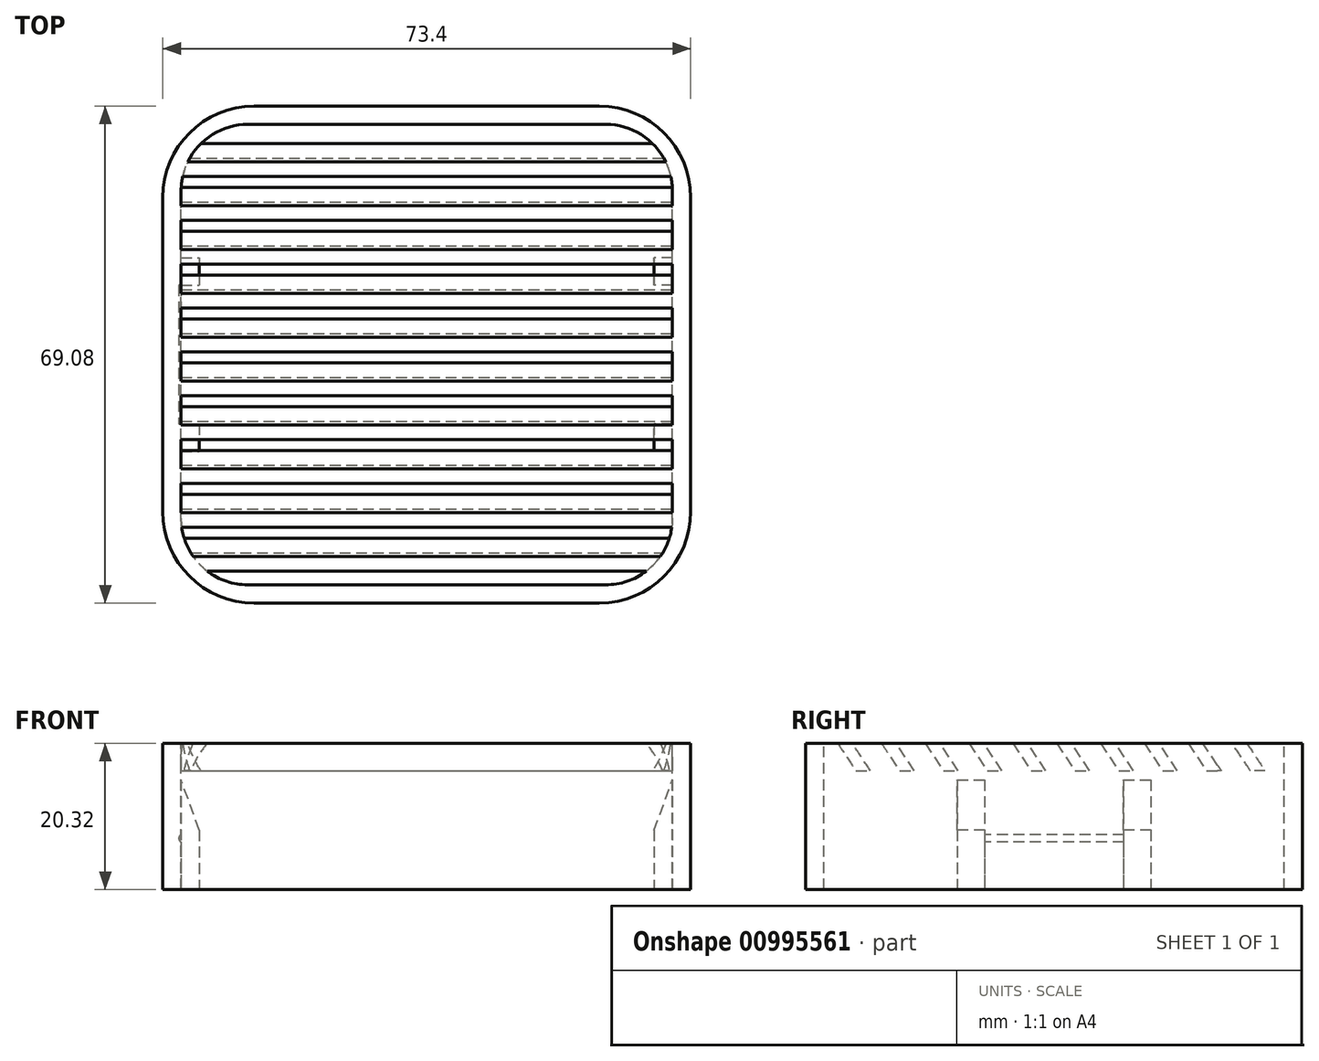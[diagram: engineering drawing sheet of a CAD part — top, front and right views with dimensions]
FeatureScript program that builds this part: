
annotation { "Feature Type Name" : "Feature", "Feature Type Description" : "" }
export const myFeature = defineFeature(function(context is Context, id is Id, definition is map)
    precondition{}
    {
        {
            var Q0;
            Q0=qCreatedBy(makeId("Top.planeOp"),FACE);
            var sketch = newSketch(context, id + "F0", { "sketchPlane" : qUnion([Q0])});
            skLineSegment(sketch, "E0.bottom", {"start": v(36.7, -34.54) * mm, "end": v(-36.7, -34.54) * mm});
            skLineSegment(sketch, "E0.top", {"start": v(36.7, 34.54) * mm, "end": v(-36.7, 34.54) * mm});
            skLineSegment(sketch, "E0.left", {"start": v(36.7, -34.54) * mm, "end": v(36.7, 34.54) * mm});
            skLineSegment(sketch, "E0.right", {"start": v(-36.7, -34.54) * mm, "end": v(-36.7, 34.54) * mm});
            skPoint(sketch, "E0.middle", {"position": v(0, 0) * mm});
            skSolve(sketch);
        }
        {
            var Q0;
            Q0=makeQuery(id+"F0.imprint","IMPRINT",FACE,{"disambiguationData":[TD([[makeQuery(id+"F0.imprint","IMPRINT",EDGE,{"derivedFrom":sQuery(id+"F0.wireOp",EDGE,"E0.bottom")}),-1.0]])]});
            extrude(context, id + "F1", {"entities" : qUnion([Q0]), "depth" : 20.32 * mm, "offsetDistance" : 25.4 * mm});
        }
        {
            var Q0;
            Q0=makeQuery(id+"F1.opExtrude","CAP_FACE",FACE,{"disambiguationData":[OSD([sQuery(id+"F0.wireOp",EDGE,"E0.bottom"),sQuery(id+"F0.wireOp",EDGE,"E0.top"),sQuery(id+"F0.wireOp",EDGE,"E0.left"),sQuery(id+"F0.wireOp",EDGE,"E0.right")])],"isStart":false});
            var sketch = newSketch(context, id + "F2", { "sketchPlane" : qUnion([Q0])});
            skLineSegment(sketch, "E1.0", {"start": v(34.16, 32) * mm, "end": v(-34.16, 32) * mm});
            skLineSegment(sketch, "E1.1", {"start": v(34.16, -32) * mm, "end": v(34.16, 32) * mm});
            skLineSegment(sketch, "E1.2", {"start": v(34.16, -32) * mm, "end": v(-34.16, -32) * mm});
            skLineSegment(sketch, "E1.3", {"start": v(-34.16, -32) * mm, "end": v(-34.16, 32) * mm});
            skSolve(sketch);
        }
        {
            var Q0;
            Q0 = qSketchRegion(id + "F2", true);
            extrude(context, id + "F3", {"entities" : qUnion([Q0]), "operationType" : NewBodyOperationType.REMOVE, "oppositeDirection" : true, "depth" : 25.4 * mm, "offsetDistance" : 25.4 * mm});
        }
        {
            var Q0;
            Q0=makeQuery(id+"F1.opExtrude","SWEPT_FACE",FACE,{"disambiguationData":[OSD([sQuery(id+"F0.wireOp",EDGE,"E0.left")])]});
            var sketch = newSketch(context, id + "F4", { "sketchPlane" : qUnion([Q0])});
            skLineSegment(sketch, "E2", {"start": v(-30.1, 20.32) * mm, "end": v(-27.56, 16.51) * mm});
            skLineSegment(sketch, "E3", {"start": v(-27.56, 16.51) * mm, "end": v(-25.53, 16.51) * mm});
            skLineSegment(sketch, "E4", {"start": v(-25.53, 16.51) * mm, "end": v(-28.07, 20.32) * mm});
            skLineSegment(sketch, "E5", {"start": v(-30.1, 20.32) * mm, "end": v(-28.07, 20.32) * mm});
            skLineSegment(sketch, "E6.1.0.0", {"start": v(-24, 20.32) * mm, "end": v(-21.46, 16.51) * mm});
            skLineSegment(sketch, "E6.1.0.1", {"start": v(-24, 20.32) * mm, "end": v(-21.97, 20.32) * mm});
            skLineSegment(sketch, "E6.1.0.2", {"start": v(-19.43, 16.51) * mm, "end": v(-21.97, 20.32) * mm});
            skLineSegment(sketch, "E6.1.0.3", {"start": v(-21.46, 16.51) * mm, "end": v(-19.43, 16.51) * mm});
            skLineSegment(sketch, "E6.2.0.0", {"start": v(-17.9, 20.32) * mm, "end": v(-15.37, 16.51) * mm});
            skLineSegment(sketch, "E6.2.0.1", {"start": v(-17.9, 20.32) * mm, "end": v(-15.87, 20.32) * mm});
            skLineSegment(sketch, "E6.2.0.2", {"start": v(-13.33, 16.51) * mm, "end": v(-15.87, 20.32) * mm});
            skLineSegment(sketch, "E6.2.0.3", {"start": v(-15.37, 16.51) * mm, "end": v(-13.33, 16.51) * mm});
            skLineSegment(sketch, "E6.3.0.0", {"start": v(-11.81, 20.32) * mm, "end": v(-9.27, 16.51) * mm});
            skLineSegment(sketch, "E6.3.0.1", {"start": v(-11.81, 20.32) * mm, "end": v(-9.78, 20.32) * mm});
            skLineSegment(sketch, "E6.3.0.2", {"start": v(-7.24, 16.51) * mm, "end": v(-9.78, 20.32) * mm});
            skLineSegment(sketch, "E6.3.0.3", {"start": v(-9.27, 16.51) * mm, "end": v(-7.24, 16.51) * mm});
            skLineSegment(sketch, "E6.4.0.0", {"start": v(-5.71, 20.32) * mm, "end": v(-3.17, 16.51) * mm});
            skLineSegment(sketch, "E6.4.0.1", {"start": v(-5.71, 20.32) * mm, "end": v(-3.68, 20.32) * mm});
            skLineSegment(sketch, "E6.4.0.2", {"start": v(-1.14, 16.51) * mm, "end": v(-3.68, 20.32) * mm});
            skLineSegment(sketch, "E6.4.0.3", {"start": v(-3.17, 16.51) * mm, "end": v(-1.14, 16.51) * mm});
            skLineSegment(sketch, "E6.5.0.0", {"start": v(0.38, 20.32) * mm, "end": v(2.92, 16.51) * mm});
            skLineSegment(sketch, "E6.5.0.1", {"start": v(0.38, 20.32) * mm, "end": v(2.41, 20.32) * mm});
            skLineSegment(sketch, "E6.5.0.2", {"start": v(4.95, 16.51) * mm, "end": v(2.41, 20.32) * mm});
            skLineSegment(sketch, "E6.5.0.3", {"start": v(2.92, 16.51) * mm, "end": v(4.95, 16.51) * mm});
            skLineSegment(sketch, "E6.6.0.0", {"start": v(6.48, 20.32) * mm, "end": v(9.02, 16.51) * mm});
            skLineSegment(sketch, "E6.6.0.1", {"start": v(6.48, 20.32) * mm, "end": v(8.5, 20.32) * mm});
            skLineSegment(sketch, "E6.6.0.2", {"start": v(11.05, 16.51) * mm, "end": v(8.5, 20.32) * mm});
            skLineSegment(sketch, "E6.6.0.3", {"start": v(9.02, 16.51) * mm, "end": v(11.05, 16.51) * mm});
            skLineSegment(sketch, "E6.7.0.0", {"start": v(12.57, 20.32) * mm, "end": v(15.11, 16.51) * mm});
            skLineSegment(sketch, "E6.7.0.1", {"start": v(12.57, 20.32) * mm, "end": v(14.6, 20.32) * mm});
            skLineSegment(sketch, "E6.7.0.2", {"start": v(17.15, 16.51) * mm, "end": v(14.6, 20.32) * mm});
            skLineSegment(sketch, "E6.7.0.3", {"start": v(15.11, 16.51) * mm, "end": v(17.15, 16.51) * mm});
            skLineSegment(sketch, "E6.8.0.0", {"start": v(18.67, 20.32) * mm, "end": v(21.2, 16.51) * mm});
            skLineSegment(sketch, "E6.8.0.1", {"start": v(18.67, 20.32) * mm, "end": v(20.7, 20.32) * mm});
            skLineSegment(sketch, "E6.8.0.2", {"start": v(23.24, 16.51) * mm, "end": v(20.7, 20.32) * mm});
            skLineSegment(sketch, "E6.8.0.3", {"start": v(21.2, 16.51) * mm, "end": v(23.24, 16.51) * mm});
            skLineSegment(sketch, "E6.9.0.0", {"start": v(24.77, 20.32) * mm, "end": v(27.3, 16.51) * mm});
            skLineSegment(sketch, "E6.9.0.1", {"start": v(24.77, 20.32) * mm, "end": v(26.8, 20.32) * mm});
            skLineSegment(sketch, "E6.9.0.2", {"start": v(29.34, 16.5) * mm, "end": v(26.8, 20.32) * mm});
            skLineSegment(sketch, "E6.9.0.3", {"start": v(27.3, 16.51) * mm, "end": v(29.34, 16.51) * mm});
            skLineSegment(sketch, "E6.direction1", {"start": v(-27.56, 16.51) * mm, "end": v(-21.46, 16.51) * mm, "construction": true});
            skSolve(sketch);
        }
        {
            var Q0;
            Q0 = qSketchRegion(id + "F4", true);
            extrude(context, id + "F5", {"entities" : qUnion([Q0]), "operationType" : NewBodyOperationType.ADD, "oppositeDirection" : true, "depth" : 73.4 * mm, "offsetDistance" : 25.4 * mm});
        }
        {
            var Q0;
            Q0=makeQuery(id+"F3.boolean.opBoolean","COPY",EDGE,{"derivedFrom":makeQuery(id+"F3.opExtrude","SWEPT_EDGE",EDGE,{"disambiguationData":[OSD([sQuery(id+"F2.wireOp",EDGE,"E1.0"),sQuery(id+"F2.wireOp",EDGE,"E1.3")])]})});
            var Q1;
            Q1=makeQuery(id+"F3.boolean.opBoolean","COPY",EDGE,{"derivedFrom":makeQuery(id+"F3.opExtrude","SWEPT_EDGE",EDGE,{"disambiguationData":[OSD([sQuery(id+"F2.wireOp",EDGE,"E1.0"),sQuery(id+"F2.wireOp",EDGE,"E1.1")])]})});
            var Q2;
            Q2=makeQuery(id+"F3.boolean.opBoolean","COPY",EDGE,{"derivedFrom":makeQuery(id+"F3.opExtrude","SWEPT_EDGE",EDGE,{"disambiguationData":[OSD([sQuery(id+"F2.wireOp",EDGE,"E1.1"),sQuery(id+"F2.wireOp",EDGE,"E1.2")])]})});
            var Q3;
            Q3=makeQuery(id+"F3.boolean.opBoolean","COPY",EDGE,{"derivedFrom":makeQuery(id+"F3.opExtrude","SWEPT_EDGE",EDGE,{"disambiguationData":[OSD([sQuery(id+"F2.wireOp",EDGE,"E1.2"),sQuery(id+"F2.wireOp",EDGE,"E1.3")])]})});
            fillet(context, id + "F6", {"entities" : qUnion([Q0, Q1, Q2, Q3]), "radius" : 9.27 * mm, "tangentPropagation" : true, "allowEdgeOverflow" : false});
        }
        {
            var Q0;
            Q0=makeQuery(id+"F1.opExtrude","SWEPT_EDGE",EDGE,{"disambiguationData":[OSD([sQuery(id+"F0.wireOp",EDGE,"E0.bottom"),sQuery(id+"F0.wireOp",EDGE,"E0.left")])]});
            var Q1;
            Q1=makeQuery(id+"F1.opExtrude","SWEPT_EDGE",EDGE,{"disambiguationData":[OSD([sQuery(id+"F0.wireOp",EDGE,"E0.top"),sQuery(id+"F0.wireOp",EDGE,"E0.left")])]});
            var Q2;
            Q2=makeQuery(id+"F1.opExtrude","SWEPT_EDGE",EDGE,{"disambiguationData":[OSD([sQuery(id+"F0.wireOp",EDGE,"E0.bottom"),sQuery(id+"F0.wireOp",EDGE,"E0.right")])]});
            var Q3;
            Q3=makeQuery(id+"F1.opExtrude","SWEPT_EDGE",EDGE,{"disambiguationData":[OSD([sQuery(id+"F0.wireOp",EDGE,"E0.top"),sQuery(id+"F0.wireOp",EDGE,"E0.right")])]});
            fillet(context, id + "F7", {"entities" : qUnion([Q0, Q1, Q2, Q3]), "radius" : 12.7 * mm, "tangentPropagation" : true, "allowEdgeOverflow" : false});
        }
        {
            var Q0;
            Q0=qCreatedBy(makeId("Front.planeOp"),FACE);
            var sketch = newSketch(context, id + "F8", { "sketchPlane" : qUnion([Q0])});
            skLineSegment(sketch, "E7", {"start": v(0, 7.62) * mm, "end": v(-34.16, 7.62) * mm});
            skCircle(sketch, "E8", {"center": v(-33.9, 7.11) * mm, "radius": 0.57 * mm});
            skCircle(sketch, "E9.MirrorC", {"center": v(33.9, 7.11) * mm, "radius": 0.57 * mm});
            skSolve(sketch);
        }
        {
            var Q0;
            {var subQ0=sQuery(id+"F8.wireOp",EDGE,"E8");var subQ1=sQuery(id+"F8.wireOp",EDGE,"E7");var subQ2=makeQuery(id+"F8.imprint","INTERSECT",VERTEX,{"disambiguationData":[OD(0.0)],"derivedFrom":[subQ1,subQ0]});Q0=makeQuery(id+"F8.imprint","IMPRINT",FACE,{"disambiguationData":[TD([[makeQuery(id+"F8.imprint","IMPRINT",EDGE,{"disambiguationData":[TD([[subQ2,1.0]])],"derivedFrom":subQ1}),1.0]])]});}
            var Q1;
            Q1=makeQuery(id+"F8.imprint","IMPRINT",FACE,{"disambiguationData":[TD([[makeQuery(id+"F8.imprint","IMPRINT",EDGE,{"derivedFrom":sQuery(id+"F8.wireOp",EDGE,"E9.MirrorC")}),-1.0]])]});
            extrude(context, id + "F9", {"entities" : qUnion([Q0, Q1]), "operationType" : NewBodyOperationType.REMOVE, "endBound" : BoundingType.SYMMETRIC, "oppositeDirection" : true, "depth" : 19.3 * mm, "offsetDistance" : 25.4 * mm});
        }
        {
            var Q0;
            Q0=makeQuery(id+"F1.opExtrude","CAP_FACE",FACE,{"disambiguationData":[OSD([sQuery(id+"F0.wireOp",EDGE,"E0.bottom"),sQuery(id+"F0.wireOp",EDGE,"E0.top"),sQuery(id+"F0.wireOp",EDGE,"E0.left"),sQuery(id+"F0.wireOp",EDGE,"E0.right")])],"isStart":true});
            var sketch = newSketch(context, id + "F10", { "sketchPlane" : qUnion([Q0])});
            skLineSegment(sketch, "E10.bottom", {"start": v(-34.16, 9.65) * mm, "end": v(-31.62, 9.65) * mm});
            skLineSegment(sketch, "E10.top", {"start": v(-34.16, 13.46) * mm, "end": v(-31.62, 13.46) * mm});
            skLineSegment(sketch, "E10.left", {"start": v(-34.16, 9.65) * mm, "end": v(-34.16, 13.46) * mm});
            skLineSegment(sketch, "E10.right", {"start": v(-31.62, 9.65) * mm, "end": v(-31.62, 13.46) * mm});
            skLineSegment(sketch, "E11.bottom", {"start": v(-34.16, -13.46) * mm, "end": v(-31.62, -13.46) * mm});
            skLineSegment(sketch, "E11.top", {"start": v(-34.16, -9.65) * mm, "end": v(-31.62, -9.65) * mm});
            skLineSegment(sketch, "E11.left", {"start": v(-34.16, -13.46) * mm, "end": v(-34.16, -9.65) * mm});
            skLineSegment(sketch, "E11.right", {"start": v(-31.62, -13.46) * mm, "end": v(-31.62, -9.65) * mm});
            skLineSegment(sketch, "E12.MirrorCS", {"start": v(31.62, 9.65) * mm, "end": v(31.62, 13.46) * mm});
            skLineSegment(sketch, "E13.MirrorCS", {"start": v(34.16, 13.46) * mm, "end": v(31.62, 13.46) * mm});
            skLineSegment(sketch, "E14.MirrorCS", {"start": v(34.16, 9.65) * mm, "end": v(34.16, 13.46) * mm});
            skLineSegment(sketch, "E15.MirrorCS", {"start": v(34.16, 9.65) * mm, "end": v(31.62, 9.65) * mm});
            skLineSegment(sketch, "E16.MirrorCS", {"start": v(34.16, -9.65) * mm, "end": v(31.62, -9.65) * mm});
            skLineSegment(sketch, "E17.MirrorCS", {"start": v(34.16, -13.46) * mm, "end": v(34.16, -9.65) * mm});
            skLineSegment(sketch, "E18.MirrorCS", {"start": v(34.16, -13.46) * mm, "end": v(31.62, -13.46) * mm});
            skLineSegment(sketch, "E19.MirrorCS", {"start": v(31.62, -13.46) * mm, "end": v(31.62, -9.65) * mm});
            skSolve(sketch);
        }
        {
            var Q0;
            Q0=makeQuery(id+"F10.imprint","IMPRINT",FACE,{"disambiguationData":[TD([[makeQuery(id+"F10.imprint","IMPRINT",EDGE,{"derivedFrom":sQuery(id+"F10.wireOp",EDGE,"E10.bottom")}),1.0]])]});
            var Q1;
            Q1=makeQuery(id+"F10.imprint","IMPRINT",FACE,{"disambiguationData":[TD([[makeQuery(id+"F10.imprint","IMPRINT",EDGE,{"derivedFrom":sQuery(id+"F10.wireOp",EDGE,"E11.bottom")}),1.0]])]});
            var Q2;
            Q2=makeQuery(id+"F10.imprint","IMPRINT",FACE,{"disambiguationData":[TD([[makeQuery(id+"F10.imprint","IMPRINT",EDGE,{"derivedFrom":sQuery(id+"F10.wireOp",EDGE,"E12.MirrorCS")}),-1.0]])]});
            var Q3;
            Q3=makeQuery(id+"F10.imprint","IMPRINT",FACE,{"disambiguationData":[TD([[makeQuery(id+"F10.imprint","IMPRINT",EDGE,{"derivedFrom":sQuery(id+"F10.wireOp",EDGE,"E16.MirrorCS")}),1.0]])]});
            extrude(context, id + "F11", {"entities" : qUnion([Q0, Q1, Q2, Q3]), "operationType" : NewBodyOperationType.ADD, "oppositeDirection" : true, "depth" : 15.24 * mm, "offsetDistance" : 25.4 * mm});
        }
        {
            var Q0;
            Q0=makeQuery(id+"F11.opExtrude","CAP_EDGE",EDGE,{"disambiguationData":[OSD([sQuery(id+"F10.wireOp",EDGE,"E10.right")])],"isStart":false});
            var Q1;
            Q1=makeQuery(id+"F11.opExtrude","CAP_EDGE",EDGE,{"disambiguationData":[OSD([sQuery(id+"F10.wireOp",EDGE,"E11.right")])],"isStart":false});
            chamfer(context, id + "F12", {"entities" : qUnion([Q0, Q1]), "chamferType" : ChamferType.TWO_OFFSETS, "width1" : 7 * mm, "oppositeDirection" : false, "width2" : 2.54 * mm, "tangentPropagation" : true});
        }
        {
            var Q0;
            Q0=makeQuery(id+"F11.opExtrude","CAP_EDGE",EDGE,{"disambiguationData":[OSD([sQuery(id+"F10.wireOp",EDGE,"E12.MirrorCS")])],"isStart":false});
            var Q1;
            Q1=makeQuery(id+"F11.opExtrude","CAP_EDGE",EDGE,{"disambiguationData":[OSD([sQuery(id+"F10.wireOp",EDGE,"E19.MirrorCS")])],"isStart":false});
            chamfer(context, id + "F13", {"entities" : qUnion([Q0, Q1]), "chamferType" : ChamferType.TWO_OFFSETS, "width1" : 2.54 * mm, "oppositeDirection" : false, "width2" : 7 * mm, "tangentPropagation" : true});
        }
    });
